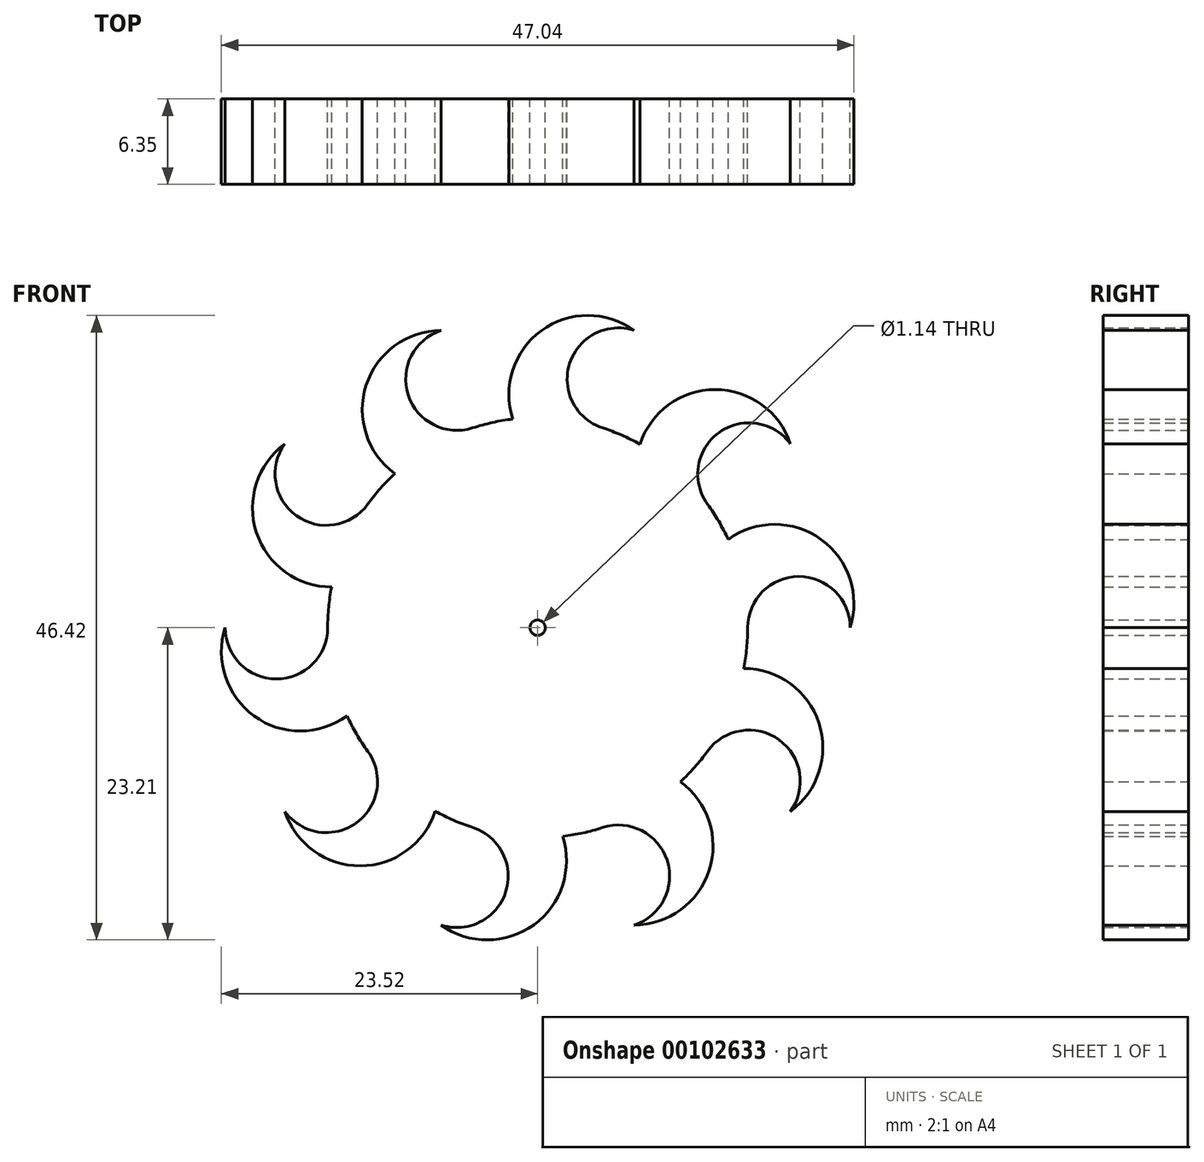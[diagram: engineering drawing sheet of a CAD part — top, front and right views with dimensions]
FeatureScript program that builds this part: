
annotation { "Feature Type Name" : "Feature", "Feature Type Description" : "" }
export const myFeature = defineFeature(function(context is Context, id is Id, definition is map)
    precondition{}
    {
        {
            var Q0;
            Q0=qCreatedBy(makeId("Front.planeOp"),FACE);
            var sketch = newSketch(context, id + "F0", { "sketchPlane" : qUnion([Q0])});
            skArc(sketch, "E0", {"start": v(14.18, 6.56) * mm, "mid": v(13.47, 7.9) * mm, "end": v(12.64, 9.18) * mm});
            skLineSegment(sketch, "E1", {"start": v(31, -8.23) * mm, "end": v(46.62, -8.23) * mm, "construction": true});
            skLineSegment(sketch, "E2", {"start": v(46.62, -8.23) * mm, "end": v(54.24, -8.23) * mm, "construction": true});
            skLineSegment(sketch, "E3", {"start": v(0, 0) * mm, "end": v(15.62, 0) * mm, "construction": true});
            skArc(sketch, "E4", {"start": v(15.62, 0) * mm, "mid": v(19.43, 3.81) * mm, "end": v(23.24, 0) * mm});
            skLineSegment(sketch, "E5", {"start": v(15.62, 0) * mm, "end": v(23.24, 0) * mm, "construction": true});
            skCircle(sketch, "E6", {"center": v(0, 0) * mm, "radius": 0.57 * mm});
            skArc(sketch, "E7", {"start": v(23.24, 0) * mm, "mid": v(21.09, 6.56) * mm, "end": v(14.18, 6.56) * mm});
            skLineSegment(sketch, "E8", {"start": v(17.63, 1.8) * mm, "end": v(19.43, 0) * mm, "construction": true});
            skArc(sketch, "E9.1.0", {"start": v(18.8, 13.66) * mm, "mid": v(13.2, 17.7) * mm, "end": v(7.61, 13.64) * mm});
            skArc(sketch, "E9.1.1", {"start": v(12.64, 9.18) * mm, "mid": v(13.48, 14.5) * mm, "end": v(18.8, 13.66) * mm});
            skArc(sketch, "E9.2.0", {"start": v(7.18, 22.1) * mm, "mid": v(0.27, 22.08) * mm, "end": v(-1.86, 15.51) * mm});
            skArc(sketch, "E9.2.1", {"start": v(4.83, 14.86) * mm, "mid": v(2.38, 19.66) * mm, "end": v(7.18, 22.1) * mm});
            skArc(sketch, "E9.3.0", {"start": v(-7.18, 22.1) * mm, "mid": v(-12.76, 18.03) * mm, "end": v(-10.62, 11.46) * mm});
            skArc(sketch, "E9.3.1", {"start": v(-4.83, 14.86) * mm, "mid": v(-9.63, 17.3) * mm, "end": v(-7.18, 22.1) * mm});
            skArc(sketch, "E9.4.0", {"start": v(-18.8, 13.66) * mm, "mid": v(-20.92, 7.08) * mm, "end": v(-15.33, 3.03) * mm});
            skArc(sketch, "E9.4.1", {"start": v(-12.64, 9.18) * mm, "mid": v(-17.96, 8.34) * mm, "end": v(-18.8, 13.66) * mm});
            skArc(sketch, "E9.5.0", {"start": v(-23.24, 0) * mm, "mid": v(-21.09, -6.56) * mm, "end": v(-14.18, -6.56) * mm});
            skArc(sketch, "E9.5.1", {"start": v(-15.62, 0) * mm, "mid": v(-19.43, -3.8) * mm, "end": v(-23.24, 0) * mm});
            skArc(sketch, "E10.trimOffspring", {"start": v(-1.86, 15.51) * mm, "mid": v(-3.36, 15.26) * mm, "end": v(-4.83, 14.86) * mm});
            skArc(sketch, "E11.trimOffspring", {"start": v(-10.62, 11.46) * mm, "mid": v(-11.68, 10.37) * mm, "end": v(-12.64, 9.18) * mm});
            skArc(sketch, "E12.trimOffspring", {"start": v(-15.33, 3.03) * mm, "mid": v(-15.55, 1.52) * mm, "end": v(-15.62, 0) * mm});
            skArc(sketch, "E13.trimOffspring", {"start": v(15.33, -3.03) * mm, "mid": v(15.55, -1.52) * mm, "end": v(15.62, 0) * mm});
            skArc(sketch, "E14.trimOffspring", {"start": v(7.61, 13.64) * mm, "mid": v(6.25, 14.32) * mm, "end": v(4.83, 14.86) * mm});
            skArc(sketch, "E15.3.6.0", {"start": v(-18.8, -13.66) * mm, "mid": v(-13.2, -17.7) * mm, "end": v(-7.61, -13.64) * mm});
            skArc(sketch, "E15.4.6.0", {"start": v(-12.64, -9.18) * mm, "mid": v(-13.48, -14.5) * mm, "end": v(-18.8, -13.66) * mm});
            skArc(sketch, "E15.3.7.0", {"start": v(-7.18, -22.1) * mm, "mid": v(-0.27, -22.08) * mm, "end": v(1.86, -15.51) * mm});
            skArc(sketch, "E15.4.7.0", {"start": v(-4.83, -14.86) * mm, "mid": v(-2.38, -19.66) * mm, "end": v(-7.18, -22.1) * mm});
            skArc(sketch, "E16.3.8.0", {"start": v(7.18, -22.1) * mm, "mid": v(12.76, -18.03) * mm, "end": v(10.62, -11.46) * mm});
            skArc(sketch, "E16.4.8.0", {"start": v(4.83, -14.86) * mm, "mid": v(9.63, -17.3) * mm, "end": v(7.18, -22.1) * mm});
            skArc(sketch, "E16.3.9.0", {"start": v(18.8, -13.66) * mm, "mid": v(20.92, -7.08) * mm, "end": v(15.33, -3.03) * mm});
            skArc(sketch, "E16.4.9.0", {"start": v(12.64, -9.18) * mm, "mid": v(17.96, -8.34) * mm, "end": v(18.8, -13.66) * mm});
            skArc(sketch, "E17.trimOffspring", {"start": v(10.62, -11.46) * mm, "mid": v(11.68, -10.37) * mm, "end": v(12.64, -9.18) * mm});
            skArc(sketch, "E18.trimOffspring", {"start": v(1.86, -15.51) * mm, "mid": v(3.36, -15.26) * mm, "end": v(4.83, -14.86) * mm});
            skArc(sketch, "E19.trimOffspring", {"start": v(-7.61, -13.64) * mm, "mid": v(-6.25, -14.32) * mm, "end": v(-4.83, -14.86) * mm});
            skArc(sketch, "E20.trimOffspring", {"start": v(-14.18, -6.56) * mm, "mid": v(-13.47, -7.9) * mm, "end": v(-12.64, -9.18) * mm});
            skSolve(sketch);
        }
        {
            var Q0;
            Q0=qSketchRegion(id+"F0",true);
            extrude(context, id + "F1", {"entities" : qUnion([Q0]), "depth" : 6.35 * mm});
        }
    });
